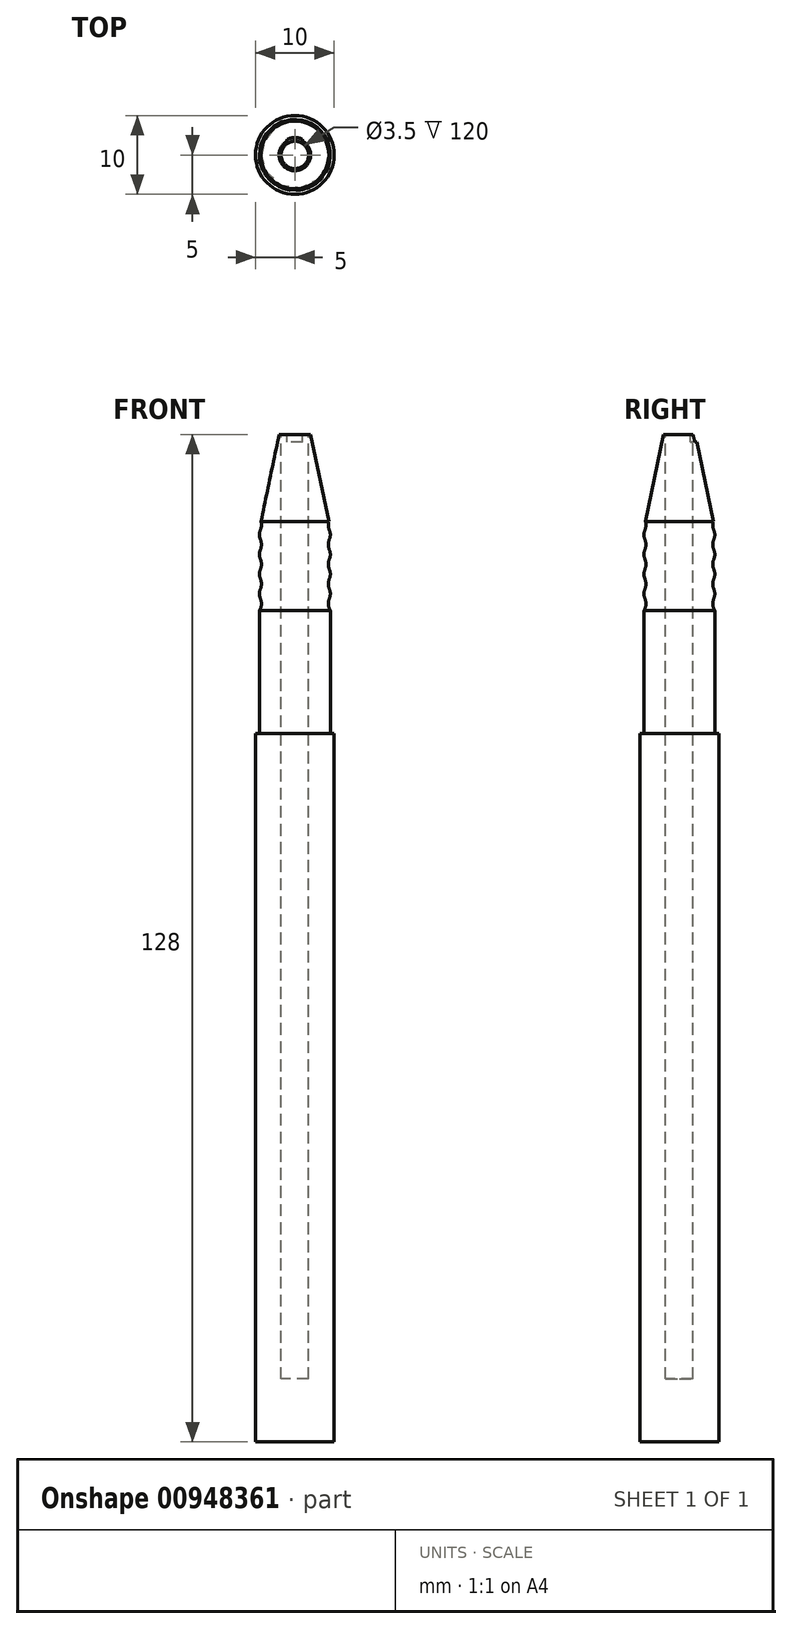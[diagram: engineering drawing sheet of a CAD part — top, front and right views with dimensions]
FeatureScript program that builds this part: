
annotation { "Feature Type Name" : "Feature", "Feature Type Description" : "" }
export const myFeature = defineFeature(function(context is Context, id is Id, definition is map)
    precondition{}
    {
        {
            var Q0;
            Q0=qCreatedBy(makeId("Top.planeOp"),FACE);
            var sketch = newSketch(context, id + "F0", { "sketchPlane" : qUnion([Q0])});
            skCircle(sketch, "E0", {"center": v(0, 0) * mm, "radius": 5 * mm});
            skSolve(sketch);
        }
        {
            var Q0;
            Q0=makeQuery(id+"F0.imprint","IMPRINT",FACE,{"disambiguationData":[TD([[makeQuery(id+"F0.imprint","IMPRINT",EDGE,{"derivedFrom":sQuery(id+"F0.wireOp",EDGE,"E0")}),1.0]])]});
            extrude(context, id + "F1", {"entities" : qUnion([Q0]), "depth" : 90 * mm, "offsetDistance" : 25 * mm});
        }
        {
            var Q0;
            Q0=makeQuery(id+"F1.opExtrude","CAP_FACE",FACE,{"disambiguationData":[OSD([sQuery(id+"F0.wireOp",EDGE,"E0")])],"isStart":false});
            var sketch = newSketch(context, id + "F2", { "sketchPlane" : qUnion([Q0])});
            skCircle(sketch, "E1", {"center": v(0, 0) * mm, "radius": 4.5 * mm});
            skSolve(sketch);
        }
        {
            var Q0;
            Q0 = qSketchRegion(id + "F2", true);
            extrude(context, id + "F3", {"entities" : qUnion([Q0]), "operationType" : NewBodyOperationType.ADD, "depth" : 26 * mm, "offsetDistance" : 25 * mm});
        }
        {
            var Q0;
            Q0=qCreatedBy(makeId("Right.planeOp"),FACE);
            var sketch = newSketch(context, id + "F4", { "sketchPlane" : qUnion([Q0])});
            skLineSegment(sketch, "E2.0", {"start": v(-4.5, 116) * mm, "end": v(4.5, 116) * mm});
            skLineSegment(sketch, "E3", {"start": v(-4.5, 116) * mm, "end": v(-2, 128) * mm});
            skLineSegment(sketch, "E4", {"start": v(-2, 128) * mm, "end": v(0, 128) * mm});
            skLineSegment(sketch, "E5", {"start": v(0, 128) * mm, "end": v(0, 116) * mm});
            skLineSegment(sketch, "E6", {"start": v(0, 116) * mm, "end": v(-4.5, 116) * mm});
            skSolve(sketch);
        }
        {
            var Q0;
            Q0 = qSketchRegion(id + "F4", true);
            var Q1;
            Q1=sQuery(id+"F4.wireOp",EDGE,"E5");
            revolve(context, id + "F5", {"operationType" : NewBodyOperationType.ADD, "surfaceOperationType" : NewSurfaceOperationType.NEW, "entities" : qUnion([Q0]), "axis" : qUnion([Q1]), "revolveType" : RevolveType.FULL});
        }
        {
            var Q0;
            Q0=qCreatedBy(makeId("Right.planeOp"),FACE);
            var sketch = newSketch(context, id + "F6", { "sketchPlane" : qUnion([Q0])});
            skLineSegment(sketch, "E7", {"start": v(-4.5, 105) * mm, "end": v(-4.5, 106.5) * mm});
            skLineSegment(sketch, "E8", {"start": v(-4.5, 106.5) * mm, "end": v(-6, 106.5) * mm});
            skCircle(sketch, "E9", {"center": v(-6, 106.5) * mm, "radius": 1.75 * mm});
            skLineSegment(sketch, "E10", {"start": v(-6, 106.5) * mm, "end": v(-6, 109) * mm});
            skCircle(sketch, "E11", {"center": v(-6, 109) * mm, "radius": 1.75 * mm});
            skLineSegment(sketch, "E12", {"start": v(-6, 109) * mm, "end": v(-6, 111.5) * mm});
            skCircle(sketch, "E13", {"center": v(-6, 111.5) * mm, "radius": 1.75 * mm});
            skLineSegment(sketch, "E14", {"start": v(-6, 111.5) * mm, "end": v(-6, 114) * mm});
            skCircle(sketch, "E15", {"center": v(-6, 114) * mm, "radius": 1.75 * mm});
            skLineSegment(sketch, "E16", {"start": v(-6, 114) * mm, "end": v(-6, 116.5) * mm});
            skCircle(sketch, "E17", {"center": v(-6, 116.5) * mm, "radius": 1.75 * mm});
            skSolve(sketch);
        }
        {
            var Q0;
            Q0 = qSketchRegion(id + "F6", true);
            var Q1;
            Q1=sQuery(id+"F4.wireOp",EDGE,"E5");
            revolve(context, id + "F7", {"operationType" : NewBodyOperationType.REMOVE, "surfaceOperationType" : NewSurfaceOperationType.NEW, "entities" : qUnion([Q0]), "axis" : qUnion([Q1]), "revolveType" : RevolveType.FULL, "oppositeDirection" : true});
        }
        {
            var Q0;
            {var subQ0=sQuery(id+"F6.wireOp",EDGE,"E9");var subQ1=sQuery(id+"F6.wireOp",EDGE,"E11");Q0=makeQuery(id+"F7.boolean.opBoolean","SPLIT",FACE,{"disambiguationData":[TD([makeQuery(id+"F7.opRevolve","SWEPT_FACE",FACE,{"disambiguationData":[OSD([subQ0])]}),makeQuery(id+"F7.opRevolve","SWEPT_FACE",FACE,{"disambiguationData":[OSD([subQ1]),TDD([makeQuery(id+"F6.imprint","IMPRINT",EDGE,{"disambiguationData":[TD([[makeQuery(id+"F6.imprint","INTERSECT",VERTEX,{"disambiguationData":[OD(0.0)],"derivedFrom":[subQ0,subQ1]}),-1.0]])],"derivedFrom":subQ1})])]})])],"derivedFrom":makeQuery(id+"F3.opExtrude","SWEPT_FACE",FACE,{"disambiguationData":[OSD([sQuery(id+"F2.wireOp",EDGE,"E1")])]})});}
            var Q1;
            {var subQ0=sQuery(id+"F6.wireOp",EDGE,"E11");var subQ1=sQuery(id+"F6.wireOp",EDGE,"E13");var subQ2=makeQuery(id+"F6.imprint","INTERSECT",VERTEX,{"disambiguationData":[OD(0.0)],"derivedFrom":[subQ0,subQ1]});Q1=makeQuery(id+"F7.boolean.opBoolean","SPLIT",FACE,{"disambiguationData":[TD([makeQuery(id+"F7.opRevolve","SWEPT_FACE",FACE,{"disambiguationData":[OSD([subQ0]),TDD([makeQuery(id+"F6.imprint","IMPRINT",EDGE,{"disambiguationData":[TD([[makeQuery(id+"F6.imprint","INTERSECT",VERTEX,{"disambiguationData":[OD(0.0)],"derivedFrom":[sQuery(id+"F6.wireOp",EDGE,"E9"),subQ0]}),-1.0]])],"derivedFrom":subQ0})])]}),makeQuery(id+"F7.opRevolve","SWEPT_FACE",FACE,{"disambiguationData":[OSD([subQ1]),TDD([makeQuery(id+"F6.imprint","IMPRINT",EDGE,{"disambiguationData":[TD([[subQ2,-1.0]])],"derivedFrom":subQ1})])]})])],"derivedFrom":makeQuery(id+"F3.opExtrude","SWEPT_FACE",FACE,{"disambiguationData":[OSD([sQuery(id+"F2.wireOp",EDGE,"E1")])]})});}
            var Q2;
            {var subQ0=sQuery(id+"F6.wireOp",EDGE,"E13");var subQ1=sQuery(id+"F6.wireOp",EDGE,"E15");var subQ2=makeQuery(id+"F6.imprint","INTERSECT",VERTEX,{"disambiguationData":[OD(0.0)],"derivedFrom":[subQ0,subQ1]});Q2=makeQuery(id+"F7.boolean.opBoolean","SPLIT",FACE,{"disambiguationData":[TD([makeQuery(id+"F7.opRevolve","SWEPT_FACE",FACE,{"disambiguationData":[OSD([subQ0]),TDD([makeQuery(id+"F6.imprint","IMPRINT",EDGE,{"disambiguationData":[TD([[makeQuery(id+"F6.imprint","INTERSECT",VERTEX,{"disambiguationData":[OD(0.0)],"derivedFrom":[sQuery(id+"F6.wireOp",EDGE,"E11"),subQ0]}),-1.0]])],"derivedFrom":subQ0})])]}),makeQuery(id+"F7.opRevolve","SWEPT_FACE",FACE,{"disambiguationData":[OSD([subQ1]),TDD([makeQuery(id+"F6.imprint","IMPRINT",EDGE,{"disambiguationData":[TD([[subQ2,-1.0]])],"derivedFrom":subQ1})])]})])],"derivedFrom":makeQuery(id+"F3.opExtrude","SWEPT_FACE",FACE,{"disambiguationData":[OSD([sQuery(id+"F2.wireOp",EDGE,"E1")])]})});}
            var Q3;
            {var subQ0=sQuery(id+"F6.wireOp",EDGE,"E15");var subQ1=sQuery(id+"F6.wireOp",EDGE,"E17");Q3=makeQuery(id+"F7.boolean.opBoolean","SPLIT",FACE,{"disambiguationData":[TD([makeQuery(id+"F7.opRevolve","SWEPT_FACE",FACE,{"disambiguationData":[OSD([subQ0]),TDD([makeQuery(id+"F6.imprint","IMPRINT",EDGE,{"disambiguationData":[TD([[makeQuery(id+"F6.imprint","INTERSECT",VERTEX,{"disambiguationData":[OD(0.0)],"derivedFrom":[sQuery(id+"F6.wireOp",EDGE,"E13"),subQ0]}),-1.0]])],"derivedFrom":subQ0})])]}),makeQuery(id+"F7.opRevolve","SWEPT_FACE",FACE,{"disambiguationData":[OSD([subQ1])]})])],"derivedFrom":makeQuery(id+"F3.opExtrude","SWEPT_FACE",FACE,{"disambiguationData":[OSD([sQuery(id+"F2.wireOp",EDGE,"E1")])]})});}
            fillet(context, id + "F8", {"entities" : qUnion([Q0, Q1, Q2, Q3]), "radius" : 1.5 * mm, "tangentPropagation" : true, "allowEdgeOverflow" : false});
        }
        {
            var Q0;
            Q0=makeQuery(id+"F5.opRevolve","SWEPT_FACE",FACE,{"disambiguationData":[OSD([sQuery(id+"F4.wireOp",EDGE,"E4")])]});
            var sketch = newSketch(context, id + "F9", { "sketchPlane" : qUnion([Q0])});
            skCircle(sketch, "E18", {"center": v(0, 0) * mm, "radius": 1.75 * mm});
            skSolve(sketch);
        }
        {
            var Q0;
            Q0 = qSketchRegion(id + "F9", true);
            extrude(context, id + "F10", {"entities" : qUnion([Q0]), "operationType" : NewBodyOperationType.REMOVE, "oppositeDirection" : true, "depth" : 120 * mm, "offsetDistance" : 25 * mm});
        }
        {
            var Q0;
            Q0=qCreatedBy(makeId("Front.planeOp"),FACE);
            var sketch = newSketch(context, id + "F11", { "sketchPlane" : qUnion([Q0])});
            skLineSegment(sketch, "E19", {"start": v(0, 127) * mm, "end": v(1, 127) * mm});
            skLineSegment(sketch, "E20", {"start": v(1, 127) * mm, "end": v(1, 128) * mm});
            skLineSegment(sketch, "E21", {"start": v(0, 127) * mm, "end": v(-1, 127) * mm});
            skLineSegment(sketch, "E22", {"start": v(-1, 127) * mm, "end": v(-1, 128) * mm});
            skLineSegment(sketch, "E23", {"start": v(-1, 128) * mm, "end": v(1, 128) * mm});
            skSolve(sketch);
        }
        {
            var Q0;
            Q0 = qSketchRegion(id + "F11", true);
            extrude(context, id + "F12", {"entities" : qUnion([Q0]), "operationType" : NewBodyOperationType.REMOVE, "oppositeDirection" : true, "depth" : 25 * mm, "offsetDistance" : 25 * mm});
        }
    });
